# Revit family: 64412219
name_source: partatom
category: Plumbing Fixtures
revit_build: Autodesk Revit 2018 (Build: 20170223_1515(x64)
units: mm (PartAtom-declared; Revit-internal decimal feet)

## family parameters
Always vertical = Yes
Cut with Voids When Loaded = No
OmniClass Number = 23.45.55.00
OmniClass Title = Sanitary Faucets, Wastes
Part Type = Normal
Room Calculation Point = No
Round Connector Dimension = Use Diameter
Shared = No
Work Plane-Based = No

## types (1)
- 64412219 Washbasin faucet, 6 V, Bluetooth
    2D/3D/BIM Files URL = http://static.hansa.com
    3D View = https://static.hansa.com
    Advanced Features = Software settings adjustable via App;Convertible for cold or premixed-water supply
    Aerator = PCA® - constant flow rate regardless of pressure variations;Standard aerator
    Afterflow Period = 3 s (1-20 s)
    Ambience photo = http://static.hansa.com
    AssetType = Fixed
    Automatic Flush Frequency = off (off/1-120 h)
    Automatic Flush Period = 30 s (1-1800 s)
    BIMObjectName = 64412219
    Backflow Prevention EN1717 = AA
    Battery = Lithium 2CR5 6 V
    Bluetooth = 4.x
    BodyMaterial = Brass
    Brand = HANSA
    Catalog Drawing URL = http://static.hansa.com
    Category = Bathroom;Public & Semi-public
    CloseOffRating = 0
    Color = Chrome
    Connection = Flexible inlet pipes
    Connection Size = G3/8
    Constituents = Single lever
    Dimension Drawing URL = http://static.hansa.com
    DurationUnit = Year
    EAN Number = 4057304014079
    EMC Directive = 2014/53/EU , 2011/65/EU
    EN Standard = EN 15091
    ETIM Class Number = EC010340 Electronic tap
    Electronic Parts = Autofocus infrared sensor;Solenoid valve;Low battery indicator
    Excluded Items = Without pop-up waste;Without draw-rod opening
    FDV Document URL = http://www.hansa.com
    FaucetMainMaterial = Brass
    Features = Touchless;Bluetooth®;Battery-operated
    Finish = Polished
    Flow Drawing URL = http://static.hansa.com
    Flow Rate At 300kPa With Flow Controller = 0.1 L/s
    FlowCoefficient = 0
    Group = Washbasin faucet
    IfcExportAs = IfcValveType
    IfcExportType = FAUCET
    InletConnectionSize = 10 mm  [stored 0.0328084 ft]
    Installation Type = Deck mounted
    Installation and Maintenance Guide URL = http://static.hansa.com
    Interactive AR View URL = https://static.hansa.com
    Lever Handle = Temperature control handle
    Manufacturer = HANSA
    ManufacturerName = HANSA
    ManufacturerURL = http://www.hansa.com
    Market = Austria;Belgium;Czech Republic;Germany;Spain;France;International;Italy;Netherlands;Slovakia
    Material = Brass
    Max Flow Period = 2 min (1 - 1800 s)
    Max. Hot Water Supply = 70 °C
    Mechanical Parts = Non-return valve(s);Litter filter(s);Mixing valve for manual temperature control
    Mobile Product Information URL = http://mpi.hansa.com
    Model = 64412219 Washbasin faucet, 6 V, Bluetooth
    ModelReference = 64412219
    Mounting Holes = 1 hole
    NBSDescription = Water supply fittings for wash basins and troughs
    NBSReference = 45-35-70/371
    Name = 64412219 Washbasin faucet, 6 V, Bluetooth
    Name_en = 64412219 Washbasin faucet, 6 V, Bluetooth
    Noise Class = I (ISO 3822)
    NominalDepth = 140 mm  [stored 0.459318 ft]
    NominalHeight = 121 mm
    NominalWidth = 65 mm
    Operating Distance = 20-130 mm (110/130/160 mm)
    Operating Voltage = 6 V
    Pressure Loss With Flow 01ls = 200000.0 Pa
    Product Code = 64412219
    Product Family = HANSAELECTRA
    Product Image URL = http://static.hansa.com
    Product URL = http://static.hansa.com
    Protection Class = IP 55
    Revision = 3
    Sales Package dimensions (LxWxH) = 290 x 210 x 90
    Shape = Sculptured
    Size = 65x140x120 mm
    Spare-Part Information URL = http://static.hansa.com
    Spout Projection = 96 mm
    Spout Type = Fixed spout;Casted construction
    Surface treatment = Chrome
    Technical DataSheet URL = http://www.hansa.com
    Temperature = Temperature fixable
    Temperature Adjustments = Temperature preset fixable
    UNSPSC Class Number = 30181700 Faucets or taps
    URL Declaration of Conformity = http://static.hansa.com
    URL REACH = http://static.hansa.com
    URL UN38.3 = http://www.hansa.com
    URL WEEE = http://www.hansa.com
    Uniclass2 = Pr_40_30_96_96
    Uniclass2015Description = Washbasin manual water supply sets
    Uniclass2015Reference = Pr_40_20_87_96
    Version = 3
    VersionDate = 01/07/2022
    Warranty Information URL = http://warranty.hansa.com
    WarrantyDescription = http://warranty.hansa.com
    WarrantyDurationUnit = Year
    Working Pressure = 50 - 1000 kPa
    WorkingPressure = 50 - 1000 kPa

note: [stored X ft] marks values corroborated as IEEE doubles in the binary element streams (Revit-internal decimal feet)

## geometry (parser evidence)
native form markers: Sweep x5
no freeform markers — native parametric forms only
